# Revit family: Artek_Chairs_Rival Chair_Rival Chair KG002
name_source: partatom
category: Furniture
revit_build: Autodesk Revit 2017 (Build: 20190508_0315(x64)
units: mm (PartAtom-declared; Revit-internal decimal feet)

## family parameters
Always vertical = Yes
Cut with Voids When Loaded = No
OmniClass Number = 23.40.20.14.14.11
OmniClass Title = Chairs
Room Calculation Point = No
Shared = No
Work Plane-Based = No

## types (1)
- Rival Chair KG002
    AssetType = Movable
    BIMObjectName = Artek_Chairs_Rival Chair_Rival Chair KG002
    Brand = Artek
    Category = Chairs
    Collection = Rival Chair
    Color = Natural Birch
    Cost = 0 $
    Description = The graceful lines of the Rival Chair mean it swivels effortlessly from office to dining table.
    Designer = Konstantin Grcic
    DurationUnit = Years
    Features = Swiveling seat
    HighestSeatingHeight = 460 mm  [stored 1.50919 ft]
    IfcExportAs = IfcFurnishingElementType
    IfcExportType = CHAIR
    LowestSeatingHeight = 460 mm  [stored 1.50919 ft]
    MainColor = Natural Birch
    Manufacturer = Artek
    ManufacturerName = Artek
    ManufacturerURL = https://www.artek.fi
    Material = Wood, leather and textile.
    Model = Rival Chair KG002
    ModelNumber = 28104100
    NBSDescription = Domestic chairs
    NBSReference = 45-35-20/365
    Name = Rival Chair KG002
    NominalDepth = 524 mm
    NominalLength = 599 mm
    ProductDatasheet = https://www.artek.fi
    ProductInformation = Konstantin Grcic’s Rival Chair represents a fresh approach to the wooden chair.
    Revision = 1
    SeatingHeight = 460 mm  [stored 1.50919 ft]
    Shape = Sculptured
    Size = 590x780x520 mm
    URL = https://www.artek.fi
    Uniclass2 = Pr_40_50_12_48
    Uniclass2015Description = Dining chairs
    Uniclass2015Reference = Pr_40_50_12_22
    Version = 1
    VersionDate = 12/11/2020

note: [stored X ft] marks values corroborated as IEEE doubles in the binary element streams (Revit-internal decimal feet)

## geometry (parser evidence)
native form markers: Sweep x4
no freeform markers — native parametric forms only
